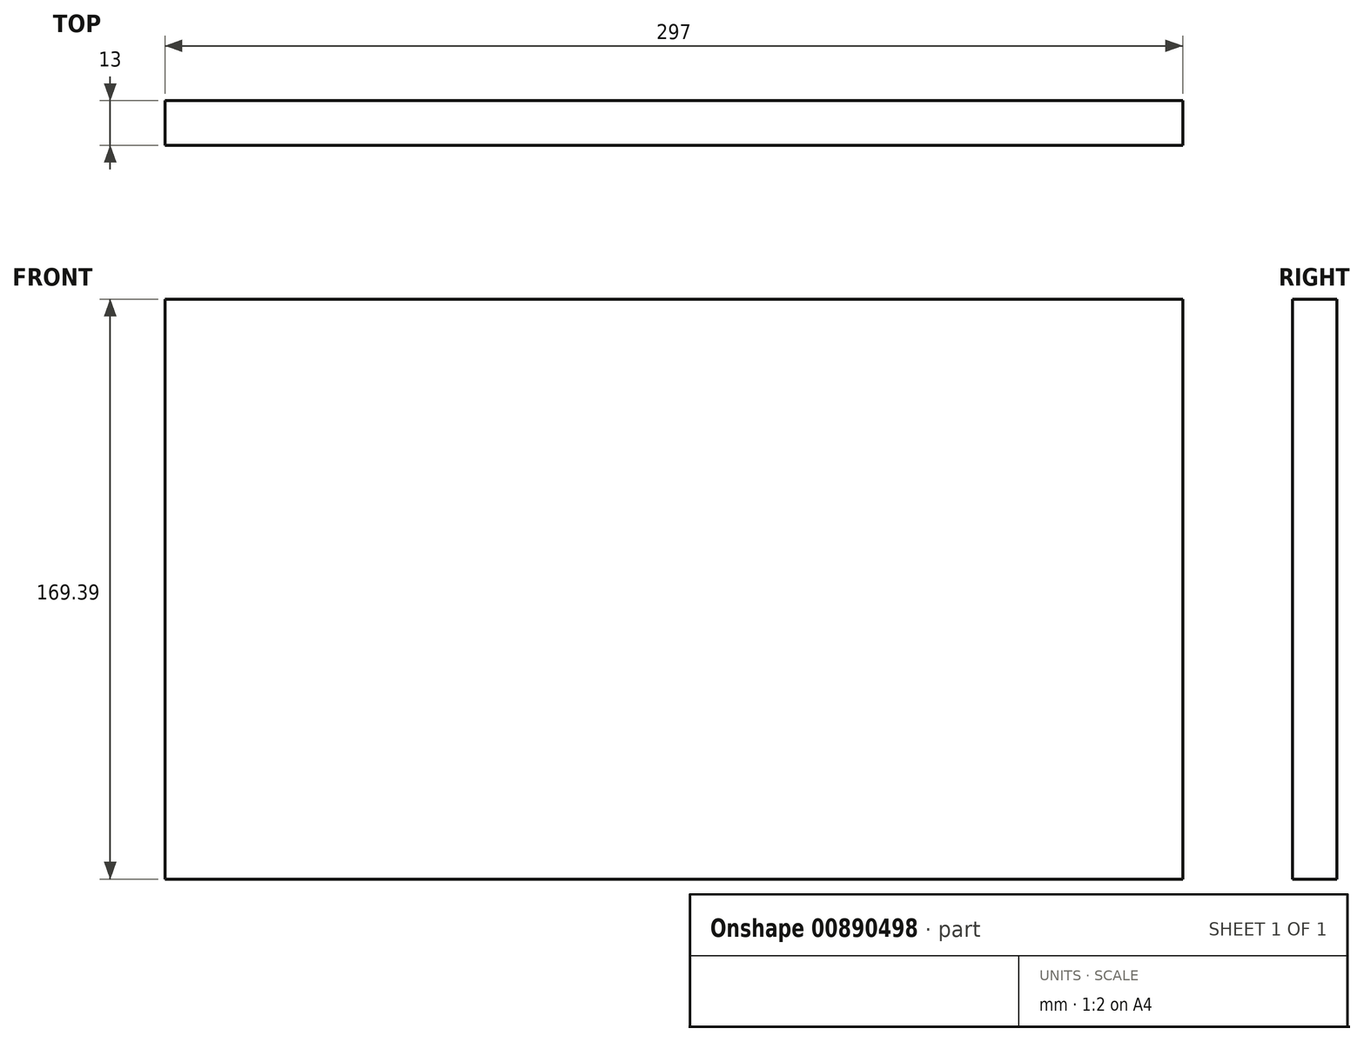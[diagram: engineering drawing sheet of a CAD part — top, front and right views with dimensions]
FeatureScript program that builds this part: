
annotation { "Feature Type Name" : "Feature", "Feature Type Description" : "" }
export const myFeature = defineFeature(function(context is Context, id is Id, definition is map)
    precondition{}
    {
        {
            var Q0;
            Q0=qCreatedBy(makeId("Front.planeOp"),FACE);
            var sketch = newSketch(context, id + "F0", { "sketchPlane" : qUnion([Q0])});
            skLineSegment(sketch, "E0.bottom", {"start": v(-152.58, 84.52) * mm, "end": v(144.42, 84.52) * mm});
            skLineSegment(sketch, "E0.top", {"start": v(-152.58, -84.87) * mm, "end": v(144.42, -84.87) * mm});
            skLineSegment(sketch, "E0.left", {"start": v(-152.58, 84.52) * mm, "end": v(-152.58, -84.87) * mm});
            skLineSegment(sketch, "E0.right", {"start": v(144.42, 84.52) * mm, "end": v(144.42, -84.87) * mm});
            skSolve(sketch);
        }
        {
            var Q0;
            Q0 = qSketchRegion(id + "F0", true);
            extrude(context, id + "F1", {"entities" : qUnion([Q0]), "depth" : 13 * mm, "offsetDistance" : 25 * mm});
        }
    });
